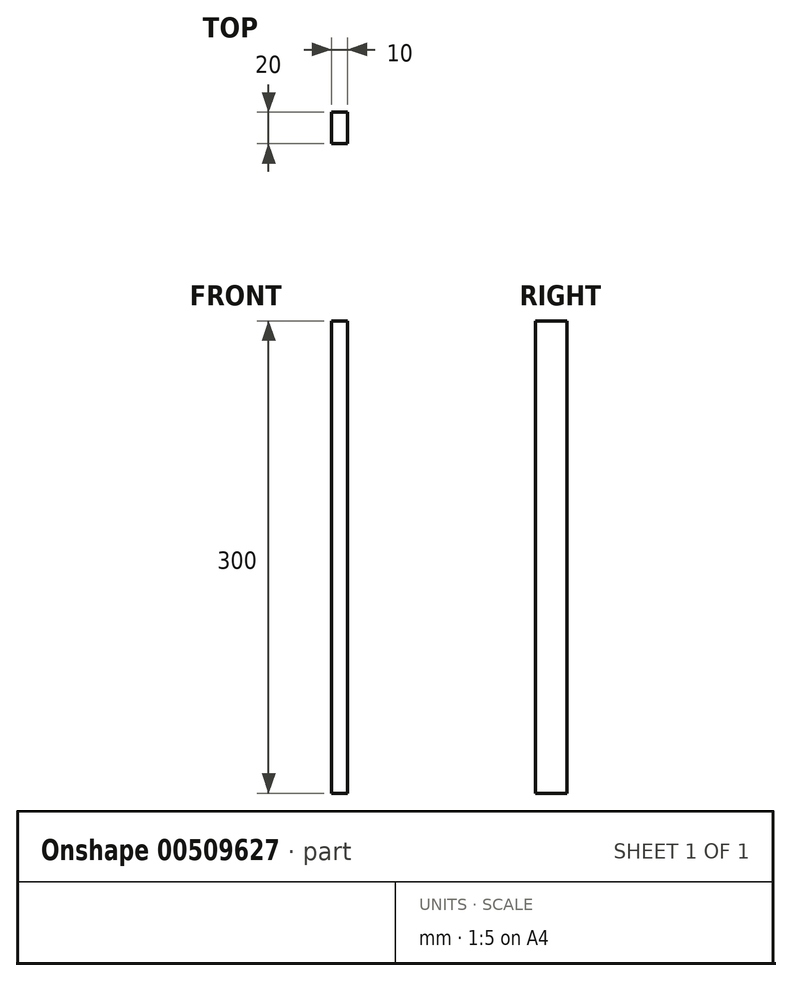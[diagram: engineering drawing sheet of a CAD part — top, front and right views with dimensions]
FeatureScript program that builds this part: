
annotation { "Feature Type Name" : "Feature", "Feature Type Description" : "" }
export const myFeature = defineFeature(function(context is Context, id is Id, definition is map)
    precondition{}
    {
        {
            var Q0;
            Q0=qCreatedBy(makeId("Top.planeOp"),FACE);
            var sketch = newSketch(context, id + "F0", { "sketchPlane" : qUnion([Q0])});
            skLineSegment(sketch, "E0.bottom", {"start": v(5, 10) * mm, "end": v(-5, 10) * mm});
            skLineSegment(sketch, "E0.top", {"start": v(5, -10) * mm, "end": v(-5, -10) * mm});
            skLineSegment(sketch, "E0.left", {"start": v(5, 10) * mm, "end": v(5, -10) * mm});
            skLineSegment(sketch, "E0.right", {"start": v(-5, 10) * mm, "end": v(-5, -10) * mm});
            skPoint(sketch, "E0.middle", {"position": v(0, 0) * mm});
            skSolve(sketch);
        }
        {
            var Q0;
            Q0=makeQuery(id+"F0.imprint","IMPRINT",FACE,{"disambiguationData":[TD([[makeQuery(id+"F0.imprint","IMPRINT",EDGE,{"derivedFrom":sQuery(id+"F0.wireOp",EDGE,"E0.bottom")}),1.0]])]});
            extrude(context, id + "F1", {"entities" : qUnion([Q0]), "depth" : 300 * mm, "offsetDistance" : 25 * mm});
        }
    });
